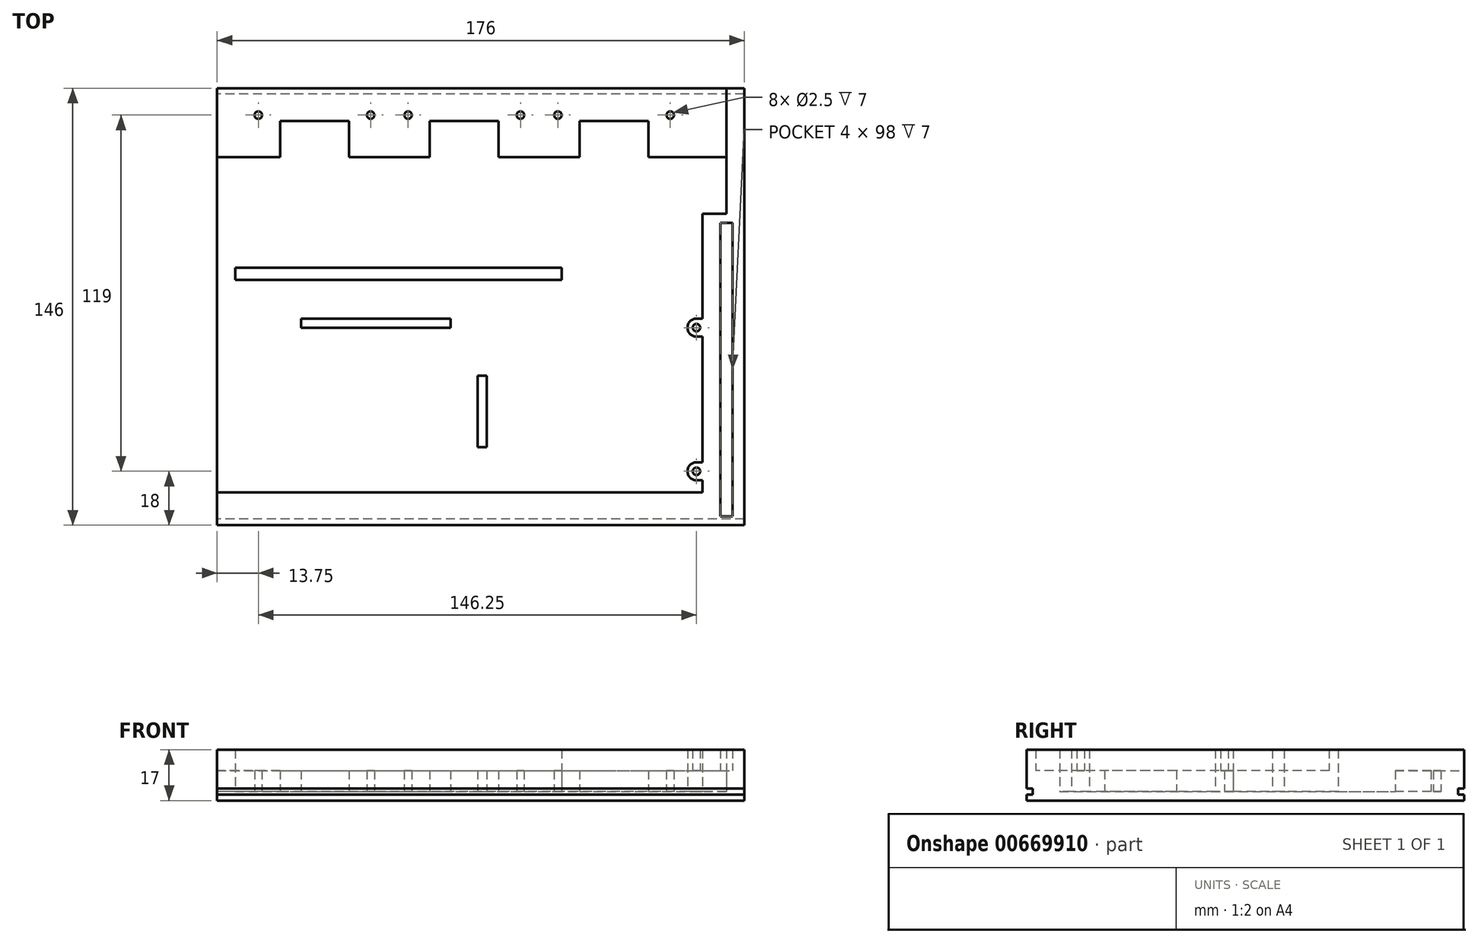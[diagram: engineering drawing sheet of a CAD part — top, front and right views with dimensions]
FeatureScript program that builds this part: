
annotation { "Feature Type Name" : "Feature", "Feature Type Description" : "" }
export const myFeature = defineFeature(function(context is Context, id is Id, definition is map)
    precondition{}
    {
        {
            var Q0;
            Q0=qCreatedBy(makeId("Top.planeOp"),FACE);
            var sketch = newSketch(context, id + "F0", { "sketchPlane" : qUnion([Q0])});
            skLineSegment(sketch, "E0.bottom", {"start": v(0, 0) * mm, "end": v(176, 0) * mm});
            skLineSegment(sketch, "E0.top", {"start": v(0, 146) * mm, "end": v(176, 146) * mm});
            skLineSegment(sketch, "E0.left", {"start": v(0, 0) * mm, "end": v(0, 146) * mm});
            skLineSegment(sketch, "E0.right", {"start": v(176, 0) * mm, "end": v(176, 146) * mm});
            skSolve(sketch);
        }
        {
            var Q0;
            Q0 = qSketchRegion(id + "F0", true);
            extrude(context, id + "F1", {"entities" : qUnion([Q0]), "depth" : 3 * mm, "offsetDistance" : 25 * mm});
        }
        {
            var Q0;
            Q0=makeQuery(id+"F1.opExtrude","CAP_FACE",FACE,{"disambiguationData":[OSD([sQuery(id+"F0.wireOp",EDGE,"E0.bottom"),sQuery(id+"F0.wireOp",EDGE,"E0.top"),sQuery(id+"F0.wireOp",EDGE,"E0.left"),sQuery(id+"F0.wireOp",EDGE,"E0.right")])],"isStart":false});
            var sketch = newSketch(context, id + "F2", { "sketchPlane" : qUnion([Q0])});
            skLineSegment(sketch, "E1", {"start": v(6, 123) * mm, "end": v(21, 123) * mm});
            skLineSegment(sketch, "E2", {"start": v(21, 135) * mm, "end": v(44, 135) * mm});
            skLineSegment(sketch, "E3", {"start": v(21, 135) * mm, "end": v(21, 123) * mm});
            skLineSegment(sketch, "E4", {"start": v(44, 135) * mm, "end": v(44, 123) * mm});
            skLineSegment(sketch, "E5", {"start": v(71, 135) * mm, "end": v(71, 123) * mm});
            skLineSegment(sketch, "E6", {"start": v(121, 135) * mm, "end": v(121, 123) * mm});
            skLineSegment(sketch, "E7", {"start": v(144, 135) * mm, "end": v(144, 123) * mm});
            skLineSegment(sketch, "E8", {"start": v(94, 135) * mm, "end": v(94, 123) * mm});
            skLineSegment(sketch, "E9.trimOffspring", {"start": v(44, 123) * mm, "end": v(71, 123) * mm});
            skLineSegment(sketch, "E10.trimOffspring", {"start": v(71, 135) * mm, "end": v(94, 135) * mm});
            skLineSegment(sketch, "E11.trimOffspring", {"start": v(94, 123) * mm, "end": v(121, 123) * mm});
            skLineSegment(sketch, "E12.trimOffspring", {"start": v(121, 135) * mm, "end": v(144, 135) * mm});
            skLineSegment(sketch, "E13.trimOffspring", {"start": v(144, 123) * mm, "end": v(170, 123) * mm});
            skLineSegment(sketch, "E14", {"start": v(6, 86) * mm, "end": v(115, 86) * mm});
            skLineSegment(sketch, "E15", {"start": v(115, 86) * mm, "end": v(115, 82) * mm});
            skLineSegment(sketch, "E16", {"start": v(115, 82) * mm, "end": v(6, 82) * mm});
            skLineSegment(sketch, "E17.bottom", {"start": v(28, 66) * mm, "end": v(78, 66) * mm});
            skLineSegment(sketch, "E17.top", {"start": v(28, 69) * mm, "end": v(78, 69) * mm});
            skLineSegment(sketch, "E17.left", {"start": v(28, 66) * mm, "end": v(28, 69) * mm});
            skLineSegment(sketch, "E17.right", {"start": v(78, 66) * mm, "end": v(78, 69) * mm});
            skLineSegment(sketch, "E18.bottom", {"start": v(87, 50) * mm, "end": v(90, 50) * mm});
            skLineSegment(sketch, "E18.top", {"start": v(87, 26) * mm, "end": v(90, 26) * mm});
            skLineSegment(sketch, "E18.left", {"start": v(87, 50) * mm, "end": v(87, 26) * mm});
            skLineSegment(sketch, "E18.right", {"start": v(90, 50) * mm, "end": v(90, 26) * mm});
            skLineSegment(sketch, "E19", {"start": v(170, 104) * mm, "end": v(162, 104) * mm});
            skLineSegment(sketch, "E20.trimOffspring", {"start": v(170, 104) * mm, "end": v(170, 123) * mm});
            skLineSegment(sketch, "E21", {"start": v(0, 137) * mm, "end": v(176, 137) * mm, "construction": true});
            skLineSegment(sketch, "E22", {"start": v(151.25, 141.14) * mm, "end": v(151.25, 134.53) * mm, "construction": true});
            skLineSegment(sketch, "E23", {"start": v(113.75, 141.14) * mm, "end": v(113.75, 134.53) * mm, "construction": true});
            skLineSegment(sketch, "E24", {"start": v(101.25, 139.9) * mm, "end": v(101.25, 133.3) * mm, "construction": true});
            skLineSegment(sketch, "E25", {"start": v(63.75, 141.14) * mm, "end": v(63.75, 133.3) * mm, "construction": true});
            skLineSegment(sketch, "E26", {"start": v(51.25, 141.27) * mm, "end": v(51.25, 133.3) * mm, "construction": true});
            skLineSegment(sketch, "E27", {"start": v(13.75, 141.41) * mm, "end": v(13.75, 133.3) * mm, "construction": true});
            skCircle(sketch, "E28", {"center": v(13.75, 137) * mm, "radius": 1.25 * mm});
            skCircle(sketch, "E29", {"center": v(51.25, 137) * mm, "radius": 1.25 * mm});
            skCircle(sketch, "E30", {"center": v(101.25, 137) * mm, "radius": 1.25 * mm});
            skCircle(sketch, "E31", {"center": v(113.75, 137) * mm, "radius": 1.25 * mm});
            skCircle(sketch, "E32", {"center": v(151.25, 137) * mm, "radius": 1.25 * mm});
            skCircle(sketch, "E33", {"center": v(63.75, 137) * mm, "radius": 1.25 * mm});
            skLineSegment(sketch, "E34", {"start": v(6, 123) * mm, "end": v(0, 123) * mm});
            skLineSegment(sketch, "E35", {"start": v(6, 82) * mm, "end": v(6, 86) * mm});
            skLineSegment(sketch, "E36", {"start": v(162, 11) * mm, "end": v(0, 11) * mm});
            skLineSegment(sketch, "E37", {"start": v(0, 123) * mm, "end": v(0, 0) * mm});
            skLineSegment(sketch, "E38", {"start": v(162, 104) * mm, "end": v(162, 69) * mm});
            skLineSegment(sketch, "E39", {"start": v(149.64, 66) * mm, "end": v(165.84, 66) * mm, "construction": true});
            skLineSegment(sketch, "E40", {"start": v(150.23, 18) * mm, "end": v(169.23, 18) * mm, "construction": true});
            skLineSegment(sketch, "E41", {"start": v(160, 73.54) * mm, "end": v(160, 6.8) * mm, "construction": true});
            skArc(sketch, "E42", {"start": v(160, 69) * mm, "mid": v(157, 66) * mm, "end": v(160, 63) * mm});
            skArc(sketch, "E43", {"start": v(160, 21) * mm, "mid": v(157, 18) * mm, "end": v(160, 15) * mm});
            skLineSegment(sketch, "E44", {"start": v(160, 21) * mm, "end": v(162, 21) * mm});
            skLineSegment(sketch, "E45", {"start": v(160, 15) * mm, "end": v(162, 15) * mm});
            skLineSegment(sketch, "E46", {"start": v(160, 63) * mm, "end": v(162, 63) * mm});
            skPoint(sketch, "E46.endSnap0", {"position": v(162, 57.5) * mm});
            skLineSegment(sketch, "E47", {"start": v(160, 69) * mm, "end": v(162, 69) * mm});
            skLineSegment(sketch, "E48.trimOffspring", {"start": v(162, 15) * mm, "end": v(162, 11) * mm});
            skLineSegment(sketch, "E49", {"start": v(162, 63) * mm, "end": v(162, 21) * mm});
            skSolve(sketch);
        }
        {
            var Q0;
            Q0=makeQuery(id+"F2.imprint","IMPRINT",FACE,{"disambiguationData":[TD([[makeQuery(id+"F2.imprint","IMPRINT",EDGE,{"derivedFrom":sQuery(id+"F2.wireOp",EDGE,"GCcvD5yt-sbKC-3Bm9-6pfF-NUPZk29DV49l.bottom")}),-1.0]])]});
            var Q1;
            Q1=makeQuery(id+"F2.imprint","IMPRINT",FACE,{"disambiguationData":[TD([[makeQuery(id+"F2.imprint","IMPRINT",EDGE,{"derivedFrom":sQuery(id+"F2.wireOp",EDGE,"E17.bottom")}),1.0]])]});
            var Q2;
            Q2=makeQuery(id+"F2.imprint","IMPRINT",FACE,{"disambiguationData":[TD([[makeQuery(id+"F2.imprint","IMPRINT",EDGE,{"derivedFrom":sQuery(id+"F2.wireOp",EDGE,"E18.bottom")}),-1.0]])]});
            var Q3;
            Q3=makeQuery(id+"F2.imprint","IMPRINT",FACE,{"disambiguationData":[TD([[makeQuery(id+"F2.imprint","IMPRINT",EDGE,{"derivedFrom":sQuery(id+"F2.wireOp",EDGE,"E14")}),-1.0]])]});
            var Q4;
            Q4=makeQuery(id+"F2.imprint","IMPRINT",FACE,{"disambiguationData":[TD([[makeQuery(id+"F2.imprint","IMPRINT",EDGE,{"derivedFrom":sQuery(id+"F2.wireOp",EDGE,"E1")}),1.0]])]});
            extrude(context, id + "F3", {"entities" : qUnion([Q0, Q1, Q2, Q3, Q4]), "operationType" : NewBodyOperationType.ADD, "depth" : 7 * mm, "offsetDistance" : 25 * mm});
        }
        {
            var Q0;
            Q0=makeQuery(id+"F3.opExtrude","CAP_FACE",FACE,{"disambiguationData":[OSD([sQuery(id+"F0.wireOp",EDGE,"E0.bottom"),sQuery(id+"F0.wireOp",EDGE,"E0.top"),sQuery(id+"F0.wireOp",EDGE,"E0.left"),sQuery(id+"F0.wireOp",EDGE,"E0.right"),sQuery(id+"F2.wireOp",EDGE,"GCcvD5yt-sbKC-3Bm9-6pfF-NUPZk29DV49l.bottom"),sQuery(id+"F2.wireOp",EDGE,"GCcvD5yt-sbKC-3Bm9-6pfF-NUPZk29DV49l.left"),sQuery(id+"F2.wireOp",EDGE,"GCcvD5yt-sbKC-3Bm9-6pfF-NUPZk29DV49l.right"),sQuery(id+"F2.wireOp",EDGE,"E1"),sQuery(id+"F2.wireOp",EDGE,"E2"),sQuery(id+"F2.wireOp",EDGE,"E3"),sQuery(id+"F2.wireOp",EDGE,"E4"),sQuery(id+"F2.wireOp",EDGE,"E5"),sQuery(id+"F2.wireOp",EDGE,"E6"),sQuery(id+"F2.wireOp",EDGE,"E7"),sQuery(id+"F2.wireOp",EDGE,"E8"),sQuery(id+"F2.wireOp",EDGE,"E9.trimOffspring"),sQuery(id+"F2.wireOp",EDGE,"E10.trimOffspring"),sQuery(id+"F2.wireOp",EDGE,"E11.trimOffspring"),sQuery(id+"F2.wireOp",EDGE,"E12.trimOffspring"),sQuery(id+"F2.wireOp",EDGE,"E13.trimOffspring"),sQuery(id+"F2.wireOp",EDGE,"E14"),sQuery(id+"F2.wireOp",EDGE,"E15"),sQuery(id+"F2.wireOp",EDGE,"E16"),sQuery(id+"F2.wireOp",EDGE,"FzcMAirM-nE30-eEYf-M1SR-h7AhY0hk5VYo"),sQuery(id+"F2.wireOp",EDGE,"saS7btnB-RKgd-JVR5-P4MM-eeiKnUnByiMc"),sQuery(id+"F2.wireOp",EDGE,"aa34dfa3-160e-4d26-b94b-15e3d075fef3.trimOffspring"),sQuery(id+"F2.wireOp",EDGE,"E19"),sQuery(id+"F2.wireOp",EDGE,"UW1zfzZ2-5hPo-yvfM-Q19C-VVyRpONFsuui"),sQuery(id+"F2.wireOp",EDGE,"uKk6Hf1I-goEQ-EOvW-dff2-RAl0EEIKsCOH"),sQuery(id+"F2.wireOp",EDGE,"E20.trimOffspring")])],"isStart":false});
            var sketch = newSketch(context, id + "F4", { "sketchPlane" : qUnion([Q0])});
            skLineSegment(sketch, "E50.bottom", {"start": v(168, 101) * mm, "end": v(172, 101) * mm});
            skLineSegment(sketch, "E50.top", {"start": v(168, 3) * mm, "end": v(172, 3) * mm});
            skLineSegment(sketch, "E50.left", {"start": v(168, 101) * mm, "end": v(168, 3) * mm});
            skLineSegment(sketch, "E50.right", {"start": v(172, 101) * mm, "end": v(172, 3) * mm});
            skCircle(sketch, "E51", {"center": v(160, 66) * mm, "radius": 1.25 * mm});
            skCircle(sketch, "E52", {"center": v(160, 18) * mm, "radius": 1.25 * mm});
            skLineSegment(sketch, "E53", {"start": v(170, 123) * mm, "end": v(170, 146) * mm});
            skSolve(sketch);
        }
        {
            var Q0;
            {var subQ1=sQuery(id+"F4.wireOp",EDGE,"fhajNLfY-DRBE-QLhE-F6I2-TTEAn2FBoYOk");Q0=makeQuery(id+"F4.imprint","IMPRINT",FACE,{"disambiguationData":[TD([[makeQuery(id+"F4.imprint","IMPRINT",EDGE,{"derivedFrom":subQ1}),-1.0]])]});}
            var Q1;
            Q1=makeQuery(id+"F3.opExtrude","CAP_FACE",FACE,{"disambiguationData":[OSD([sQuery(id+"F2.wireOp",EDGE,"E14"),sQuery(id+"F2.wireOp",EDGE,"E15"),sQuery(id+"F2.wireOp",EDGE,"E16"),sQuery(id+"F2.wireOp",EDGE,"E35")])],"isStart":false});
            var Q2;
            Q2=makeQuery(id+"F4.imprint","IMPRINT",FACE,{"disambiguationData":[TD([[makeQuery(id+"F4.imprint","IMPRINT",EDGE,{"derivedFrom":sQuery(id+"F4.wireOp",EDGE,"E50.bottom")}),1.0]])]});
            extrude(context, id + "F5", {"entities" : qUnion([Q0, Q1, Q2]), "operationType" : NewBodyOperationType.ADD, "depth" : 7 * mm, "offsetDistance" : 25 * mm});
        }
        {
            var Q0;
            {var subQ0=sQuery(id+"F2.wireOp",EDGE,"E37");var subQ1=sQuery(id+"F0.wireOp",EDGE,"E0.left");Q0=makeQuery(id+"F5.boolean.opBoolean","MERGE",FACE,{"derivedFrom":[makeQuery(id+"F3.boolean.opBoolean","MERGE",FACE,{"derivedFrom":[makeQuery(id+"F1.opExtrude","SWEPT_FACE",FACE,{"disambiguationData":[OSD([subQ1])]}),makeQuery(id+"F3.opExtrude","SWEPT_FACE",FACE,{"disambiguationData":[OSD([subQ0])]}),makeQuery(id+"F3.opExtrude","SWEPT_FACE",FACE,{"disambiguationData":[OSD([subQ1])]})]}),makeQuery(id+"F5.opExtrude","SWEPT_FACE",FACE,{"disambiguationData":[OSD([subQ0])]})]});}
            var sketch = newSketch(context, id + "F6", { "sketchPlane" : qUnion([Q0])});
            skLineSegment(sketch, "E54.bottom", {"start": v(-146, 4) * mm, "end": v(-144, 4) * mm});
            skLineSegment(sketch, "E54.top", {"start": v(-146, 2) * mm, "end": v(-144, 2) * mm});
            skLineSegment(sketch, "E54.left", {"start": v(-146, 4) * mm, "end": v(-146, 2) * mm});
            skLineSegment(sketch, "E54.right", {"start": v(-144, 4) * mm, "end": v(-144, 2) * mm});
            skLineSegment(sketch, "E55.bottom", {"start": v(0, 4) * mm, "end": v(-2, 4) * mm});
            skLineSegment(sketch, "E55.top", {"start": v(0, 2) * mm, "end": v(-2, 2) * mm});
            skLineSegment(sketch, "E55.left", {"start": v(0, 4) * mm, "end": v(0, 2) * mm});
            skLineSegment(sketch, "E55.right", {"start": v(-2, 4) * mm, "end": v(-2, 2) * mm});
            skSolve(sketch);
        }
        {
            var Q0;
            Q0 = qSketchRegion(id + "F6", true);
            extrude(context, id + "F7", {"entities" : qUnion([Q0]), "operationType" : NewBodyOperationType.REMOVE, "oppositeDirection" : true, "depth" : 176 * mm, "offsetDistance" : 25 * mm});
        }
    });
